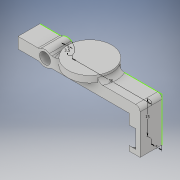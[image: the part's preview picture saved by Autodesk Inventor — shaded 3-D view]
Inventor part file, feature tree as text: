
AUTODESK INVENTOR PART (.ipt)
format: ipt  version: 2019 (Build 230136000, 136)  size: 174,080 bytes
history: native  units: in
note: dims shown in document units (in); Inventor stores cm internally (conversion verified against a paired STEP export)
features: fillet x7, sketch x4, extrude x3, hole x1
ambient origin geometry x8: Origin, YZ Plane, XZ Plane, XY Plane, X Axis, Y Axis, Z Axis, Center Point
bodies: Solid1 (feature_tree)
feature tree (15):
  sketch  "Sketch1"  dims[d6=0.1969in d7=0.1378in]
  extrude  "Extrusion1"  Depth=0.1378in
  extrude  "Extrusion2"  Depth=0.5906in
  fillet  "Fillet1"  Radius=0.1969in
  fillet  "Fillet2"  Radius=0.3937in
  fillet  "Fillet3"  Radius=0.7874in
  extrude  "Extrusion3"  Depth=0.0787in
  fillet  "Fillet4"  Radius=0.0787in
  fillet  "Fillet5"  Radius=0.0787in
  fillet  "Fillet6"  Radius=0.1181in
  fillet  "Fillet7"  Radius=0.0787in
  hole  "Hole1"  [1 undecoded]
  sketch  "Sketch2"  dims[d8=1.4173in d9=0.5906in d10=0.1969in d14=0.3937in d15=0.0in d16=0.7874in]
  sketch  "Sketch3"  dims[d17=0.1181in d18=0.0in d19=0.0787in d20=0.0787in d21=0.0787in d22=0.1181in d23=0.0in d24=0.0787in]
  sketch  "Sketch4"  dims[d25=0.0787in d26=0.0787in d27=0.0787in d28=0.0787in d29=0.2362in d30=0.1575in d31=0.0787in d32=90.0deg d33=0.0787in d34=0.8108in]
note: 1 required parameter value undecoded (feature->parameter linkage not recoverable at this tier; creation-order binding heuristic only, values carry confidence <= 0.55)
